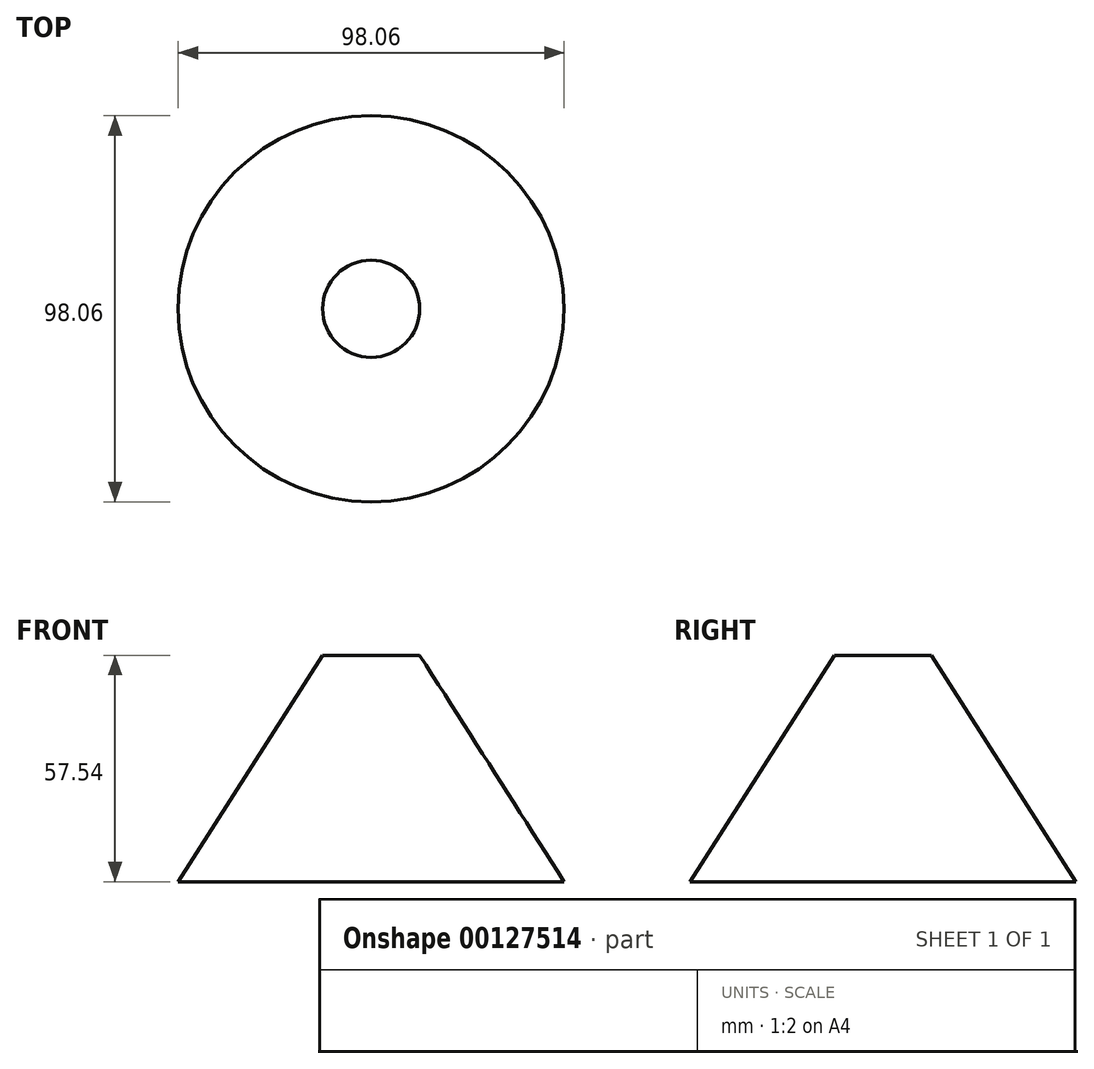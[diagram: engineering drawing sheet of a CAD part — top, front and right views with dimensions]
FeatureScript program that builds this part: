
annotation { "Feature Type Name" : "Feature", "Feature Type Description" : "" }
export const myFeature = defineFeature(function(context is Context, id is Id, definition is map)
    precondition{}
    {
        {
            var Q0;
            Q0=qCreatedBy(makeId("Front.planeOp"),FACE);
            var sketch = newSketch(context, id + "F0", { "sketchPlane" : qUnion([Q0])});
            skLineSegment(sketch, "E0", {"start": v(0, 40.37) * mm, "end": v(0, -17.76) * mm});
            skLineSegment(sketch, "E1", {"start": v(0, -17.76) * mm, "end": v(49.03, -17.76) * mm});
            skLineSegment(sketch, "E2", {"start": v(49.03, -17.76) * mm, "end": v(12.33, 39.78) * mm});
            skLineSegment(sketch, "E3", {"start": v(12.33, 39.78) * mm, "end": v(0, 39.78) * mm});
            skSolve(sketch);
        }
        {
            var Q0;
            {var subQ0=sQuery(id+"F0.wireOp",EDGE,"E1");Q0=makeQuery(id+"F0.imprint","IMPRINT",FACE,{"disambiguationData":[TD([[makeQuery(id+"F0.imprint","IMPRINT",EDGE,{"derivedFrom":subQ0}),1.0]])]});}
            var Q1;
            Q1=sQuery(id+"F0.wireOp",EDGE,"E0");
            revolve(context, id + "F1", {"entities" : qUnion([Q0]), "axis" : qUnion([Q1]), "revolveType" : RevolveType.FULL});
        }
    });
